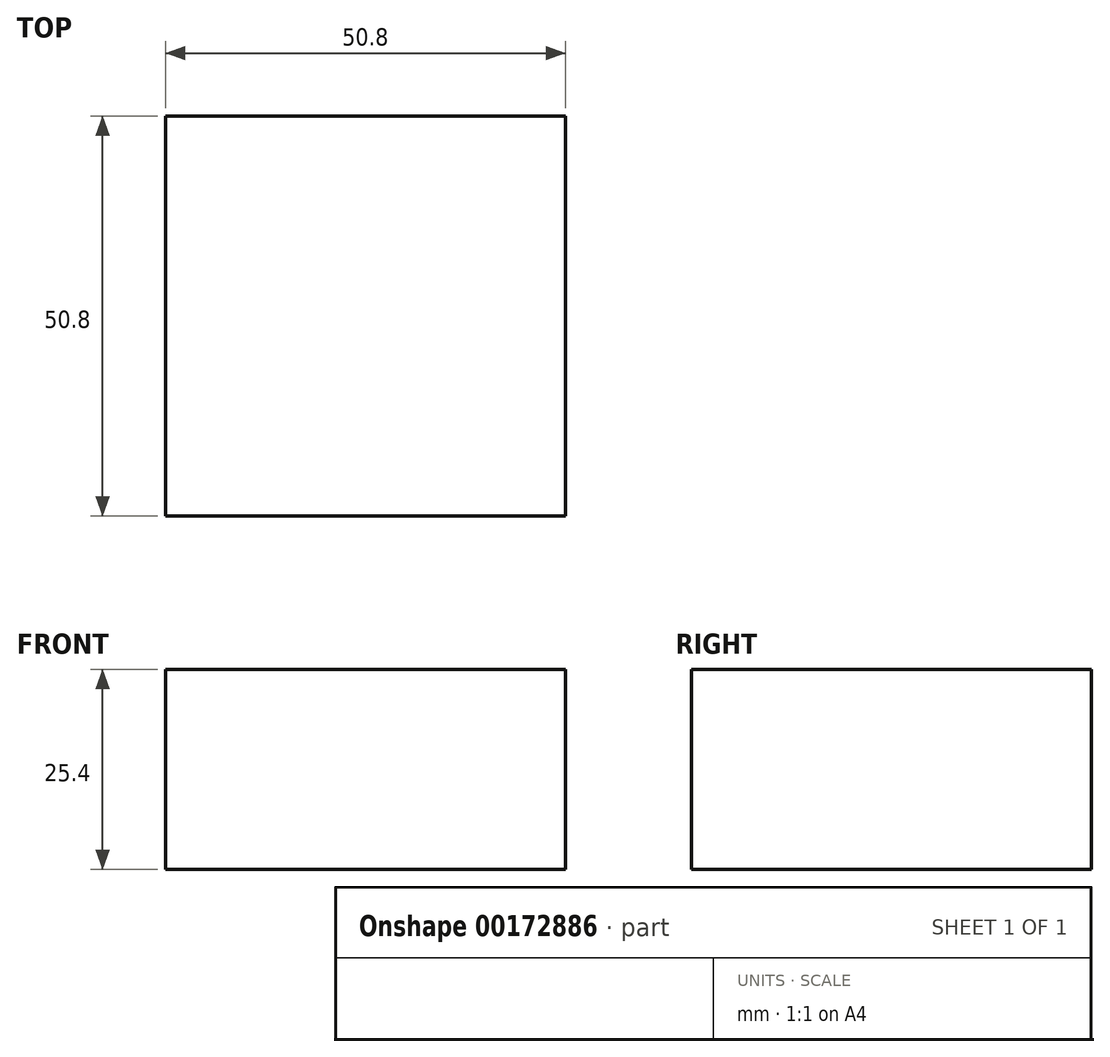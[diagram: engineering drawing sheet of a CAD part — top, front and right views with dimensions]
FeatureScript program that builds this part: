
annotation { "Feature Type Name" : "Feature", "Feature Type Description" : "" }
export const myFeature = defineFeature(function(context is Context, id is Id, definition is map)
    precondition{}
    {
        {
            var Q0;
            Q0=qCreatedBy(makeId("Top.planeOp"),FACE);
            var sketch = newSketch(context, id + "F0", { "sketchPlane" : qUnion([Q0])});
            skLineSegment(sketch, "E0.bottom", {"start": v(25.4, 25.4) * mm, "end": v(-25.4, 25.4) * mm});
            skLineSegment(sketch, "E0.top", {"start": v(25.4, -25.4) * mm, "end": v(-25.4, -25.4) * mm});
            skLineSegment(sketch, "E0.left", {"start": v(25.4, 25.4) * mm, "end": v(25.4, -25.4) * mm});
            skLineSegment(sketch, "E0.right", {"start": v(-25.4, 25.4) * mm, "end": v(-25.4, -25.4) * mm});
            skPoint(sketch, "E0.middle", {"position": v(0, 0) * mm});
            skSolve(sketch);
        }
        {
            var Q0;
            Q0=makeQuery(id+"F0.imprint","IMPRINT",FACE,{"disambiguationData":[TD([[makeQuery(id+"F0.imprint","IMPRINT",EDGE,{"derivedFrom":sQuery(id+"F0.wireOp",EDGE,"E0.bottom")}),1.0]])]});
            extrude(context, id + "F1", {"entities" : qUnion([Q0]), "depth" : 25.4 * mm});
        }
    });
